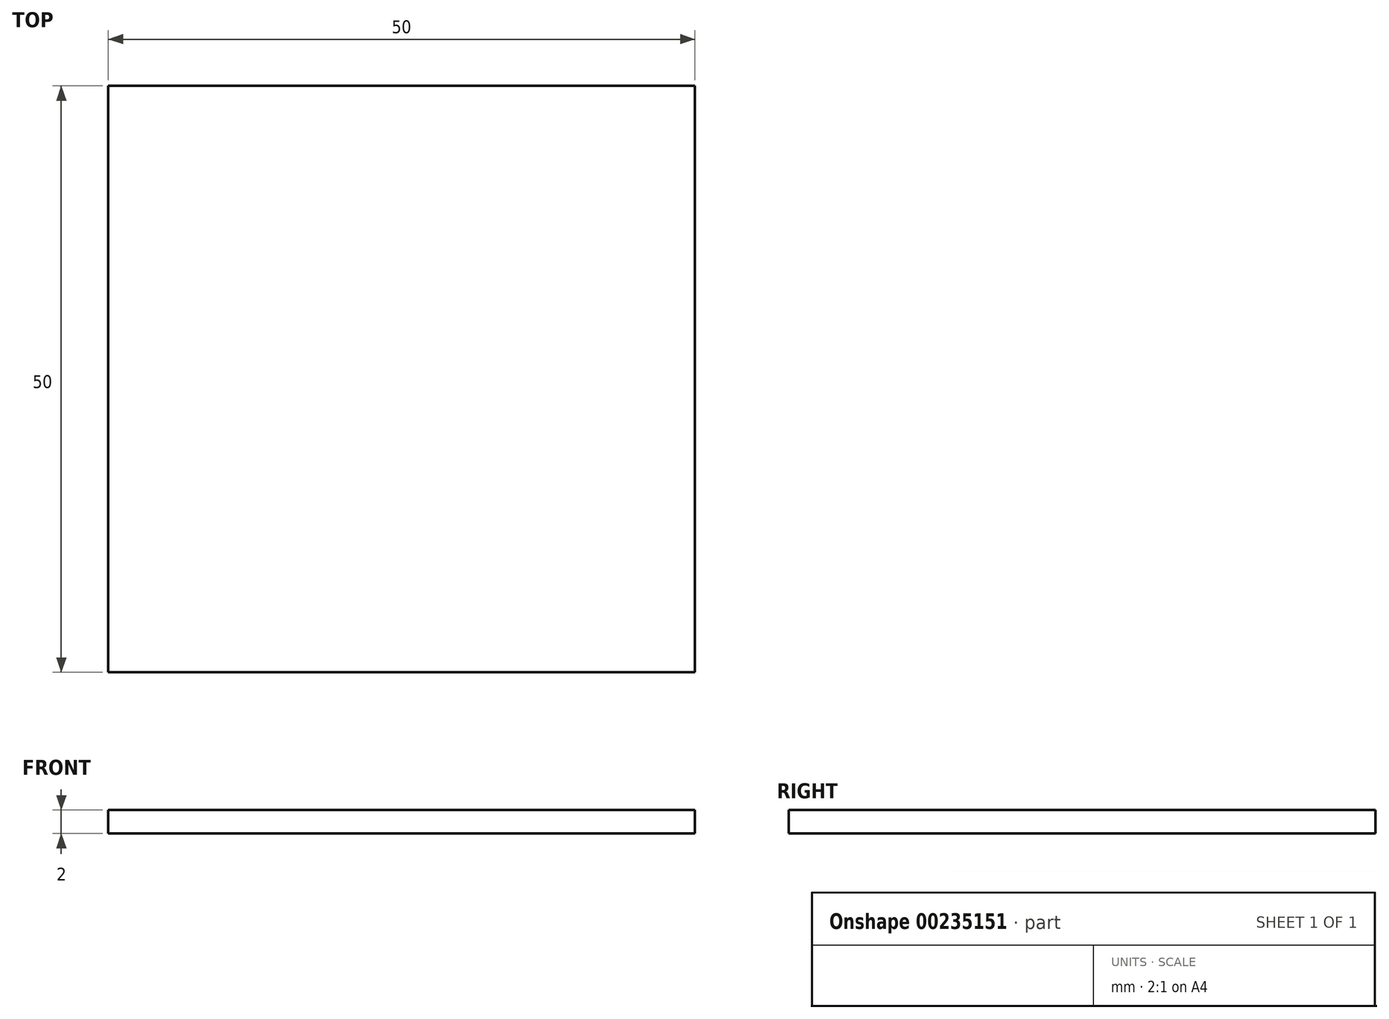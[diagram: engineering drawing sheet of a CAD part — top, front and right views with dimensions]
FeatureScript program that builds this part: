
annotation { "Feature Type Name" : "Feature", "Feature Type Description" : "" }
export const myFeature = defineFeature(function(context is Context, id is Id, definition is map)
    precondition{}
    {
        {
            var Q0;
            Q0=qCreatedBy(makeId("Top.planeOp"),FACE);
            var sketch = newSketch(context, id + "F0", { "sketchPlane" : qUnion([Q0])});
            skLineSegment(sketch, "E0.bottom", {"start": v(-22.48, 30.1) * mm, "end": v(27.52, 30.1) * mm});
            skLineSegment(sketch, "E0.top", {"start": v(-22.48, -19.9) * mm, "end": v(27.52, -19.9) * mm});
            skLineSegment(sketch, "E0.left", {"start": v(-22.48, 30.1) * mm, "end": v(-22.48, -19.9) * mm});
            skLineSegment(sketch, "E0.right", {"start": v(27.52, 30.1) * mm, "end": v(27.52, -19.9) * mm});
            skSolve(sketch);
        }
        {
            var Q0;
            Q0=makeQuery(id+"F0.imprint","IMPRINT",FACE,{"disambiguationData":[TD([[makeQuery(id+"F0.imprint","IMPRINT",EDGE,{"derivedFrom":sQuery(id+"F0.wireOp",EDGE,"E0.bottom")}),-1.0]])]});
            extrude(context, id + "F1", {"entities" : qUnion([Q0]), "depth" : 2 * mm});
        }
    });
